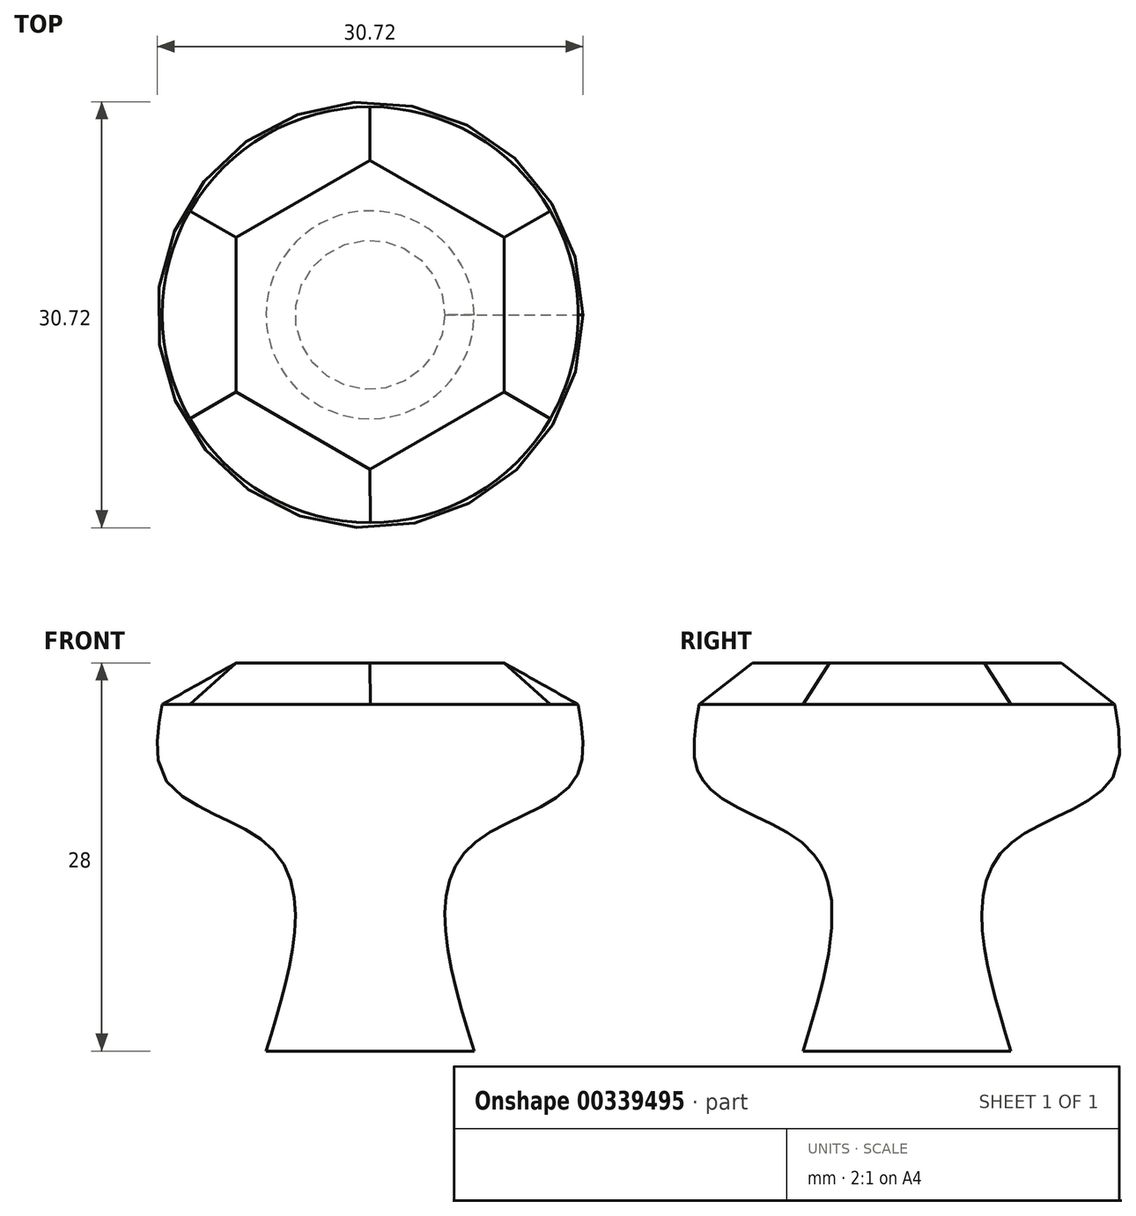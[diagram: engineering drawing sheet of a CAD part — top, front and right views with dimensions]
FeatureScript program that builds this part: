
annotation { "Feature Type Name" : "Feature", "Feature Type Description" : "" }
export const myFeature = defineFeature(function(context is Context, id is Id, definition is map)
    precondition{}
    {
        {
            var Q0;
            Q0=qCreatedBy(makeId("Top.planeOp"),FACE);
            var sketch = newSketch(context, id + "F0", { "sketchPlane" : qUnion([Q0])});
            skCircle(sketch, "E0", {"center": v(0, 0) * mm, "radius": 7.5 * mm});
            skSolve(sketch);
        }
        {
            var Q0;
            Q0=qCreatedBy(makeId("Top.planeOp"),FACE);
            cPlane(context, id + "F1", {"entities" : qUnion([Q0]), "cplaneType" : CPlaneType.OFFSET, "offset" : 25 * mm, "width" : 150 * mm, "height" : 150 * mm});
        }
        {
            var Q0;
            Q0=qCreatedBy(id+"F1.planeOp",FACE);
            var sketch = newSketch(context, id + "F2", { "sketchPlane" : qUnion([Q0])});
            skCircle(sketch, "E1", {"center": v(0, 0) * mm, "radius": 15 * mm});
            skSolve(sketch);
        }
        {
            var Q0;
            Q0=qCreatedBy(makeId("Top.planeOp"),FACE);
            cPlane(context, id + "F3", {"entities" : qUnion([Q0]), "cplaneType" : CPlaneType.OFFSET, "offset" : 15 * mm, "width" : 150 * mm, "height" : 150 * mm});
        }
        {
            var Q0;
            Q0=qCreatedBy(id+"F3.planeOp",FACE);
            var sketch = newSketch(context, id + "F4", { "sketchPlane" : qUnion([Q0])});
            skCircle(sketch, "E2", {"center": v(0, 0) * mm, "radius": 7.5 * mm});
            skSolve(sketch);
        }
        {
            var Q0;
            Q0=qCreatedBy(makeId("Top.planeOp"),FACE);
            cPlane(context, id + "F5", {"entities" : qUnion([Q0]), "cplaneType" : CPlaneType.OFFSET, "offset" : 20 * mm, "width" : 150 * mm, "height" : 150 * mm});
        }
        {
            var Q0;
            Q0=qCreatedBy(id+"F5.planeOp",FACE);
            var sketch = newSketch(context, id + "F6", { "sketchPlane" : qUnion([Q0])});
            skCircle(sketch, "E3", {"center": v(0, 0) * mm, "radius": 15 * mm});
            skSolve(sketch);
        }
        {
            var Q0;
            Q0=makeQuery(id+"F0.imprint","IMPRINT",FACE,{"disambiguationData":[TD([[makeQuery(id+"F0.imprint","IMPRINT",EDGE,{"derivedFrom":sQuery(id+"F0.wireOp",EDGE,"E0")}),1.0]])]});
            var Q1;
            Q1=makeQuery(id+"F4.imprint","IMPRINT",FACE,{"disambiguationData":[TD([[makeQuery(id+"F4.imprint","IMPRINT",EDGE,{"derivedFrom":sQuery(id+"F4.wireOp",EDGE,"E2")}),1.0]])]});
            var Q2;
            Q2=makeQuery(id+"F6.imprint","IMPRINT",FACE,{"disambiguationData":[TD([[makeQuery(id+"F6.imprint","IMPRINT",EDGE,{"derivedFrom":sQuery(id+"F6.wireOp",EDGE,"E3")}),1.0]])]});
            var Q3;
            Q3=makeQuery(id+"F2.imprint","IMPRINT",FACE,{"disambiguationData":[TD([[makeQuery(id+"F2.imprint","IMPRINT",EDGE,{"derivedFrom":sQuery(id+"F2.wireOp",EDGE,"E1")}),1.0]])]});
            loft(context, id + "F7", {"sheetProfilesArray" : [{ "sheetProfileEntities" : qUnion([Q0]) }, { "sheetProfileEntities" : qUnion([Q1]) }, { "sheetProfileEntities" : qUnion([Q2]) }, { "sheetProfileEntities" : qUnion([Q3]) }]});
        }
        {
            var Q0;
            Q0=qCreatedBy(makeId("Top.planeOp"),FACE);
            cPlane(context, id + "F9", {"entities" : qUnion([Q0]), "cplaneType" : CPlaneType.OFFSET, "offset" : 28 * mm, "width" : 150 * mm, "height" : 150 * mm});
        }
        {
            var Q0;
            Q0=qCreatedBy(id+"F9.planeOp",FACE);
            var sketch = newSketch(context, id + "F10", { "sketchPlane" : qUnion([Q0])});
            skCircle(sketch, "E4.cCircle", {"center": v(0, 0) * mm, "radius": 9.66 * mm, "construction": true});
            skLineSegment(sketch, "E4.0", {"start": v(9.66, 5.58) * mm, "end": v(9.66, -5.58) * mm});
            skLineSegment(sketch, "E4.1", {"start": v(9.66, -5.58) * mm, "end": v(0, -11.15) * mm});
            skLineSegment(sketch, "E4.2", {"start": v(0, -11.15) * mm, "end": v(-9.66, -5.58) * mm});
            skLineSegment(sketch, "E4.3", {"start": v(-9.66, -5.58) * mm, "end": v(-9.66, 5.58) * mm});
            skLineSegment(sketch, "E4.4", {"start": v(-9.66, 5.58) * mm, "end": v(0, 11.15) * mm});
            skLineSegment(sketch, "E4.5", {"start": v(0, 11.15) * mm, "end": v(9.66, 5.58) * mm});
            skPoint(sketch, "E4.0.midPoint", {"position": v(9.66, 0) * mm});
            skSolve(sketch);
        }
        {
            var Q1;
            Q1=makeQuery(id+"F7.opLoft","CAP_FACE",FACE,{"disambiguationData":[OSD([makeQuery(id+"F2.imprint","IMPRINT",FACE,{"disambiguationData":[TD([[makeQuery(id+"F2.imprint","IMPRINT",EDGE,{"derivedFrom":sQuery(id+"F2.wireOp",EDGE,"E1")}),1.0]])]})])],"isStart":true});
            var Q2;
            Q2=makeQuery(id+"F10.imprint","IMPRINT",FACE,{"disambiguationData":[TD([[makeQuery(id+"F10.imprint","IMPRINT",EDGE,{"derivedFrom":sQuery(id+"F10.wireOp",EDGE,"E4.0")}),-1.0]])]});
            loft(context, id + "F11", {"operationType" : NewBodyOperationType.ADD, "sheetProfilesArray" : [{ "sheetProfileEntities" : qUnion([Q1]) }, { "sheetProfileEntities" : qUnion([Q2]) }]});
        }
    });
